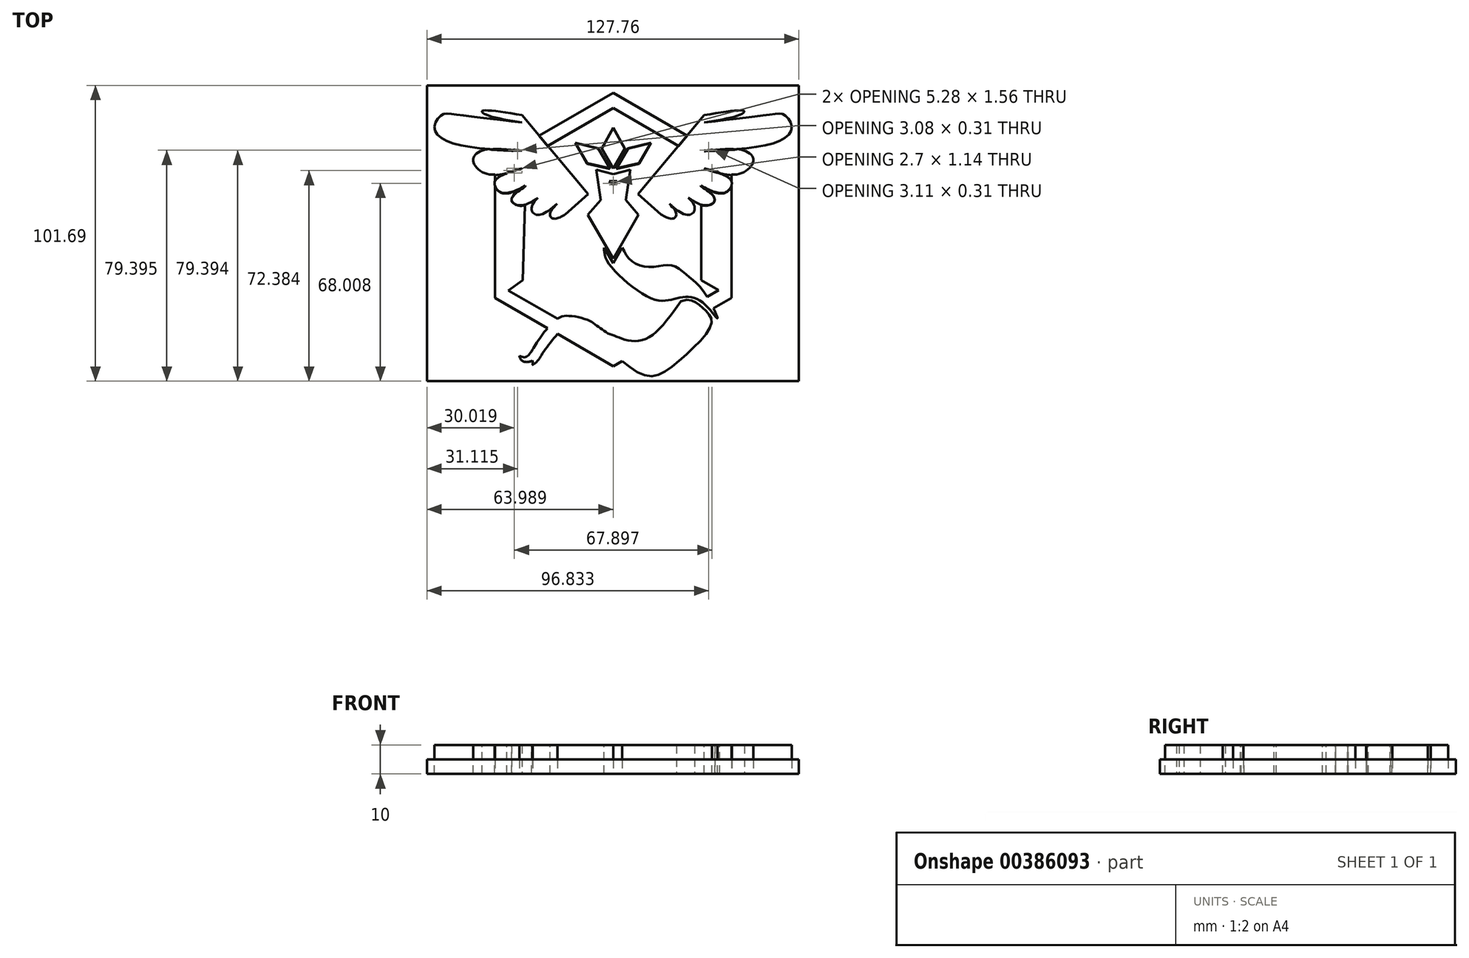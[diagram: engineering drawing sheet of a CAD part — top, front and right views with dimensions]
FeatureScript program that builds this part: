
annotation { "Feature Type Name" : "Feature", "Feature Type Description" : "" }
export const myFeature = defineFeature(function(context is Context, id is Id, definition is map)
    precondition{}
    {
        {
            var Q0;
            Q0=qCreatedBy(makeId("Top.planeOp"),FACE);
            var sketch = newSketch(context, id + "F0", { "sketchPlane" : qUnion([Q0])});
            skLineSegment(sketch, "E0.0", {"start": v(-34.42, 27.09) * mm, "end": v(-34.1, 27.27) * mm});
            skLineSegment(sketch, "E0.1", {"start": v(-0.03, 46.93) * mm, "end": v(25.45, 32.25) * mm});
            skLineSegment(sketch, "E0.2", {"start": v(40.64, 18.71) * mm, "end": v(40.62, -23.47) * mm});
            skLineSegment(sketch, "E0.3", {"start": v(40.62, -23.47) * mm, "end": v(34.43, -27.05) * mm});
            skLineSegment(sketch, "E0.4", {"start": v(-0.03, -46.93) * mm, "end": v(-19.17, -35.86) * mm});
            skLineSegment(sketch, "E0.5", {"start": v(-40.66, -23.44) * mm, "end": v(-40.66, 18.71) * mm});
            skLineSegment(sketch, "E1.1", {"start": v(-36.2, 20.89) * mm, "end": v(-36.18, 20.9) * mm});
            skLineSegment(sketch, "E1.2", {"start": v(-0.03, 41.74) * mm, "end": v(22.51, 28.74) * mm});
            skLineSegment(sketch, "E1.4", {"start": v(36.16, -20.84) * mm, "end": v(32.26, -23.1) * mm});
            skLineSegment(sketch, "E1.5", {"start": v(0.03, -41.74) * mm, "end": v(-0.03, -41.7) * mm});
            skLineSegment(sketch, "E2.0", {"start": v(-31.14, -17.38) * mm, "end": v(-30.4, 8.4) * mm});
            skLineSegment(sketch, "E2.3", {"start": v(30.15, 14.97) * mm, "end": v(30.15, 14.86) * mm});
            skLineSegment(sketch, "E3", {"start": v(-34.6, 19.99) * mm, "end": v(-34.47, 19.91) * mm});
            skLineSegment(sketch, "E4", {"start": v(-36.13, -20.9) * mm, "end": v(-31.14, -17.38) * mm});
            skLineSegment(sketch, "E5", {"start": v(36.16, -20.84) * mm, "end": v(30.18, -17.39) * mm});
            skLineSegment(sketch, "E6", {"start": v(34.42, 19.9) * mm, "end": v(34.55, 19.98) * mm});
            skLineSegment(sketch, "E7.1", {"start": v(8.6, 5.06) * mm, "end": v(-0.04, -10.05) * mm});
            skLineSegment(sketch, "E7.2", {"start": v(-0.04, -10.05) * mm, "end": v(-8.73, 5.03) * mm});
            skPoint(sketch, "E7.0.midPoint", {"position": v(-0.06, 5.04) * mm});
            skLineSegment(sketch, "E8", {"start": v(-8.73, 5.03) * mm, "end": v(-4.35, 10.2) * mm});
            skLineSegment(sketch, "E9", {"start": v(4.29, 10.2) * mm, "end": v(8.6, 5.06) * mm});
            skLineSegment(sketch, "E10", {"start": v(-0.03, 20.9) * mm, "end": v(-3.95, 27.84) * mm});
            skLineSegment(sketch, "E11", {"start": v(-3.95, 27.84) * mm, "end": v(-0.03, 34.95) * mm});
            skLineSegment(sketch, "E12", {"start": v(-0.03, 34.95) * mm, "end": v(3.92, 27.84) * mm});
            skLineSegment(sketch, "E13", {"start": v(3.92, 27.84) * mm, "end": v(-0.03, 20.9) * mm});
            skLineSegment(sketch, "E14", {"start": v(1.05, 20.86) * mm, "end": v(5.08, 27.84) * mm});
            skLineSegment(sketch, "E15", {"start": v(5.08, 27.84) * mm, "end": v(12.97, 29.67) * mm});
            skLineSegment(sketch, "E16", {"start": v(12.97, 29.67) * mm, "end": v(8.92, 22.65) * mm});
            skLineSegment(sketch, "E17", {"start": v(8.92, 22.65) * mm, "end": v(1.05, 20.86) * mm});
            skLineSegment(sketch, "E18", {"start": v(-0.03, 19.06) * mm, "end": v(5.8, 20.53) * mm});
            skLineSegment(sketch, "E19", {"start": v(5.8, 20.53) * mm, "end": v(4.29, 10.2) * mm});
            skLineSegment(sketch, "E20.MirrorCS", {"start": v(-1.11, 20.86) * mm, "end": v(-5.14, 27.84) * mm});
            skLineSegment(sketch, "E21.MirrorCS", {"start": v(36.13, 20.89) * mm, "end": v(36.12, 20.89) * mm});
            skLineSegment(sketch, "E22.MirrorCS", {"start": v(-8.98, 22.65) * mm, "end": v(-1.11, 20.86) * mm});
            skLineSegment(sketch, "E23.MirrorCS", {"start": v(-13.03, 29.67) * mm, "end": v(-8.98, 22.65) * mm});
            skLineSegment(sketch, "E24.MirrorCS", {"start": v(-5.14, 27.84) * mm, "end": v(-13.03, 29.67) * mm});
            skLineSegment(sketch, "E25.MirrorCS", {"start": v(-5.85, 20.53) * mm, "end": v(-4.35, 10.2) * mm});
            skLineSegment(sketch, "E26.MirrorCS", {"start": v(-0.03, 19.06) * mm, "end": v(-5.85, 20.53) * mm});
            skPoint(sketch, "E27.endSnap0", {"position": v(2.88, 19.8) * mm});
            skLineSegment(sketch, "E28", {"start": v(8.54, 12.07) * mm, "end": v(16.4, 5.06) * mm});
            skFitSpline(sketch, "E29", {"points": [v(16.4, 5.06) * mm, v(20.32, 3.6) * mm, v(21.7, 5.06) * mm, v(16.4, 11.34) * mm], "startDerivative": vector(12.83, -7.25) * mm, "endDerivative": vector(-17.45, 15.71) * mm});
            skFitSpline(sketch, "E30", {"points": [v(16.4, 11.34) * mm, v(24.02, 5.3) * mm, v(27.15, 5.3) * mm, v(27.86, 8) * mm, v(21.51, 14.15) * mm], "startDerivative": vector(24.54, -23.19) * mm, "endDerivative": vector(-27.7, 19.99) * mm});
            skFitSpline(sketch, "E31", {"points": [v(21.51, 14.15) * mm, v(31.76, 8.18) * mm, v(34.89, 10.17) * mm, v(27.63, 16.43) * mm], "startDerivative": vector(26.85, -21.95) * mm, "endDerivative": vector(-29.92, 18.45) * mm});
            skFitSpline(sketch, "E32", {"points": [v(27.63, 16.43) * mm, v(38.3, 12.59) * mm, v(40.63, 16.43) * mm, v(31.28, 20.89) * mm], "startDerivative": vector(31.14, -18.38) * mm, "endDerivative": vector(-35.14, 9.32) * mm});
            skFitSpline(sketch, "E33", {"points": [v(31.28, 20.89) * mm, v(43.86, 19.14) * mm, v(48.13, 23.83) * mm, v(44.57, 27.1) * mm, v(31.28, 26.96) * mm], "startDerivative": vector(45.87, -14.68) * mm, "endDerivative": vector(-48.56, -5.6) * mm});
            skFitSpline(sketch, "E34", {"points": [v(31.28, 26.96) * mm, v(57.1, 30.24) * mm, v(61.36, 35.08) * mm, v(58.94, 39.2) * mm, v(54.82, 39.49) * mm, v(31.28, 36.64) * mm], "startDerivative": vector(100.04, 4.04) * mm, "endDerivative": vector(-97.48, -11.56) * mm});
            skFitSpline(sketch, "E35", {"points": [v(31.28, 36.64) * mm, v(44.13, 39.57) * mm, v(44.99, 40.57) * mm, v(31.28, 39.2) * mm], "startDerivative": vector(37.5, 6.3) * mm, "endDerivative": vector(-44.89, -7.34) * mm});
            skFitSpline(sketch, "E36", {"points": [v(8.54, 12.07) * mm, v(31.28, 39.2) * mm], "startDerivative": vector(22.74, 27.13) * mm, "endDerivative": vector(22.74, 27.13) * mm});
            skLineSegment(sketch, "E37.trimOffspring", {"start": v(30.15, 8.44) * mm, "end": v(30.18, -17.39) * mm});
            skLineSegment(sketch, "E38.trimOffspring", {"start": v(36.12, 20.89) * mm, "end": v(36.13, 20.9) * mm});
            skLineSegment(sketch, "E39.trimOffspring", {"start": v(34.07, 27.28) * mm, "end": v(34.39, 27.1) * mm});
            skFitSpline(sketch, "E40.MirrorCS", {"points": [v(-8.6, 12.07) * mm, v(-31.34, 39.2) * mm], "startDerivative": vector(-22.74, 27.13) * mm, "endDerivative": vector(-22.74, 27.13) * mm});
            skLineSegment(sketch, "E41.MirrorCS", {"start": v(-8.6, 12.07) * mm, "end": v(-16.47, 5.06) * mm});
            skFitSpline(sketch, "E42.MirrorCS", {"points": [v(-16.47, 5.06) * mm, v(-20.38, 3.6) * mm, v(-21.76, 5.06) * mm, v(-16.47, 11.34) * mm], "startDerivative": vector(-12.83, -7.25) * mm, "endDerivative": vector(17.45, 15.71) * mm});
            skFitSpline(sketch, "E43.MirrorCS", {"points": [v(-16.47, 11.34) * mm, v(-24.08, 5.3) * mm, v(-27.21, 5.3) * mm, v(-27.93, 8) * mm, v(-21.57, 14.15) * mm], "startDerivative": vector(-24.54, -23.19) * mm, "endDerivative": vector(27.7, 19.99) * mm});
            skFitSpline(sketch, "E44.MirrorCS", {"points": [v(-21.57, 14.15) * mm, v(-31.82, 8.18) * mm, v(-34.95, 10.17) * mm, v(-27.7, 16.43) * mm], "startDerivative": vector(-26.85, -21.95) * mm, "endDerivative": vector(29.92, 18.45) * mm});
            skFitSpline(sketch, "E45.MirrorCS", {"points": [v(-27.7, 16.43) * mm, v(-38.37, 12.59) * mm, v(-40.7, 16.43) * mm, v(-31.34, 20.89) * mm], "startDerivative": vector(-31.14, -18.38) * mm, "endDerivative": vector(35.14, 9.32) * mm});
            skFitSpline(sketch, "E46.MirrorCS", {"points": [v(-31.34, 20.89) * mm, v(-43.92, 19.14) * mm, v(-48.19, 23.83) * mm, v(-44.63, 27.1) * mm, v(-31.34, 26.96) * mm], "startDerivative": vector(-45.87, -14.68) * mm, "endDerivative": vector(48.56, -5.6) * mm});
            skFitSpline(sketch, "E47.MirrorCS", {"points": [v(-31.34, 26.96) * mm, v(-57.15, 30.24) * mm, v(-61.42, 35.08) * mm, v(-59, 39.2) * mm, v(-54.88, 39.49) * mm, v(-31.34, 36.64) * mm], "startDerivative": vector(-100.04, 4.04) * mm, "endDerivative": vector(97.48, -11.56) * mm});
            skFitSpline(sketch, "E48.MirrorCS", {"points": [v(-31.34, 36.64) * mm, v(-44.2, 39.57) * mm, v(-45.05, 40.57) * mm, v(-31.34, 39.2) * mm], "startDerivative": vector(-37.5, 6.3) * mm, "endDerivative": vector(44.89, -7.34) * mm});
            skLineSegment(sketch, "E49.trimOffspring", {"start": v(-36.18, 20.9) * mm, "end": v(-36.2, 20.9) * mm});
            skLineSegment(sketch, "E50.trimOffspring", {"start": v(-25.5, 32.24) * mm, "end": v(-0.03, 46.93) * mm});
            skLineSegment(sketch, "E51.trimOffspring", {"start": v(-22.57, 28.74) * mm, "end": v(-0.03, 41.74) * mm});
            skLineSegment(sketch, "E52.trimOffspring", {"start": v(-30.2, 14.86) * mm, "end": v(-30.2, 14.97) * mm});
            skLineSegment(sketch, "E53", {"start": v(-0.03, -11.6) * mm, "end": v(3.06, -6.2) * mm});
            skLineSegment(sketch, "E54.MirrorCS", {"start": v(-0.03, -11.6) * mm, "end": v(-3.12, -6.2) * mm});
            skFitSpline(sketch, "E55", {"points": [v(3.06, -6.2) * mm, v(6.6, -11.02) * mm, v(13.43, -12.87) * mm, v(20.12, -12.3) * mm, v(25.39, -15.72) * mm, v(31.36, -21.7) * mm, v(35.78, -30.52) * mm, v(29.9, -24.46) * mm, v(20.83, -23.83) * mm], "startDerivative": vector(25.23, -49.18) * mm, "endDerivative": vector(-67.6, -14.69) * mm});
            skFitSpline(sketch, "E56", {"points": [v(20.83, -23.83) * mm, v(13.57, -23.83) * mm, v(-1.8, -11.3) * mm, v(-3.12, -6.2) * mm], "startDerivative": vector(-22.06, -5.97) * mm, "endDerivative": vector(0.15, 18.4) * mm});
            skFitSpline(sketch, "E57", {"points": [v(23.25, -24.69) * mm, v(28.58, -25.22) * mm, v(32.22, -28.32) * mm, v(33.78, -32.23) * mm, v(22.97, -44.75) * mm, v(11.01, -50.16) * mm, v(-5.4, -38.6) * mm], "startDerivative": vector(57.83, 25.3) * mm, "endDerivative": vector(-68.09, 39.24) * mm});
            skFitSpline(sketch, "E58", {"points": [v(23.25, -24.69) * mm, v(10.3, -37.92) * mm, v(2.19, -37.21) * mm, v(-1.94, -35.65) * mm], "startDerivative": vector(-29.4, -41.34) * mm, "endDerivative": vector(-18.15, 5.69) * mm});
            skLineSegment(sketch, "E59.trimOffspring", {"start": v(3.03, -45.17) * mm, "end": v(-0.03, -46.93) * mm});
            skFitSpline(sketch, "E60", {"points": [v(-1.94, -35.65) * mm, v(-5.4, -33.23) * mm, v(-8.95, -31.03) * mm, v(-16.57, -29.68) * mm, v(-19.2, -30.65) * mm], "startDerivative": vector(-15, 10.15) * mm, "endDerivative": vector(-10.84, -6.57) * mm});
            skFitSpline(sketch, "E61", {"points": [v(-19.2, -30.65) * mm, v(-21.65, -32.72) * mm, v(-26.22, -38.82) * mm, v(-28.75, -42.7) * mm, v(-30.45, -43.9) * mm, v(-32.3, -43.39) * mm], "startDerivative": vector(-12.13, -8.75) * mm, "endDerivative": vector(-13.1, 6) * mm});
            skFitSpline(sketch, "E62", {"points": [v(-32.3, -43.39) * mm, v(-31.67, -44.82) * mm, v(-29.8, -45.54) * mm, v(-27.77, -45) * mm], "startDerivative": vector(1.27, -5.16) * mm, "endDerivative": vector(5.63, 2.32) * mm});
            skFitSpline(sketch, "E63", {"points": [v(-27.77, -45) * mm, v(-27.77, -46.38) * mm, v(-27.77, -46.5) * mm, v(-26.15, -45.27) * mm, v(-24.42, -42.7) * mm, v(-19.75, -36.56) * mm, v(-16.46, -33.51) * mm, v(-12.5, -33.57) * mm, v(-5.4, -38.6) * mm], "startDerivative": vector(0.74, -21.08) * mm, "endDerivative": vector(36.31, -31.02) * mm});
            skLineSegment(sketch, "E64.trimOffspring", {"start": v(-22.64, -33.86) * mm, "end": v(-40.66, -23.44) * mm});
            skLineSegment(sketch, "E65.trimOffspring", {"start": v(-19.2, -30.65) * mm, "end": v(-36.13, -20.9) * mm});
            skLineSegment(sketch, "E66.trimOffspring", {"start": v(-0.03, -41.7) * mm, "end": v(-0.03, -42.57) * mm});
            skLineSegment(sketch, "E67", {"start": v(-0.03, 15.32) * mm, "end": v(1.32, 16.46) * mm});
            skLineSegment(sketch, "E68", {"start": v(1.32, 16.46) * mm, "end": v(-0.03, 16.46) * mm});
            skLineSegment(sketch, "E69.MirrorCS", {"start": v(-1.38, 16.46) * mm, "end": v(-0.03, 16.46) * mm});
            skLineSegment(sketch, "E70.MirrorCS", {"start": v(-0.03, 15.32) * mm, "end": v(-1.38, 16.46) * mm});
            skSolve(sketch);
        }
        {
            var Q0;
            Q0=makeQuery(id+"F0.imprint","IMPRINT",FACE,{"disambiguationData":[TD([[makeQuery(id+"F0.imprint","IMPRINT",EDGE,{"derivedFrom":sQuery(id+"F0.wireOp",EDGE,"E7.1")}),-1.0]])]});
            var Q1;
            {var subQ3=sQuery(id+"F0.wireOp",EDGE,"E53");Q1=makeQuery(id+"F0.imprint","IMPRINT",FACE,{"disambiguationData":[TD([[makeQuery(id+"F0.imprint","IMPRINT",EDGE,{"derivedFrom":subQ3}),-1.0]])]});}
            var Q2;
            {var subQ0=sQuery(id+"F0.wireOp",EDGE,"E58");Q2=makeQuery(id+"F0.imprint","IMPRINT",FACE,{"disambiguationData":[TD([[makeQuery(id+"F0.imprint","IMPRINT",EDGE,{"derivedFrom":subQ0}),1.0]])]});}
            var Q3;
            Q3=makeQuery(id+"F0.imprint","IMPRINT",FACE,{"disambiguationData":[TD([[makeQuery(id+"F0.imprint","IMPRINT",EDGE,{"derivedFrom":sQuery(id+"F0.wireOp",EDGE,"E10")}),-1.0]])]});
            var Q4;
            Q4=makeQuery(id+"F0.imprint","IMPRINT",FACE,{"disambiguationData":[TD([[makeQuery(id+"F0.imprint","IMPRINT",EDGE,{"derivedFrom":sQuery(id+"F0.wireOp",EDGE,"E20.MirrorCS")}),1.0]])]});
            var Q5;
            Q5=makeQuery(id+"F0.imprint","IMPRINT",FACE,{"disambiguationData":[TD([[makeQuery(id+"F0.imprint","IMPRINT",EDGE,{"derivedFrom":sQuery(id+"F0.wireOp",EDGE,"E14")}),-1.0]])]});
            var Q6;
            {var subQ4=sQuery(id+"F0.wireOp",EDGE,"E0.1");Q6=makeQuery(id+"F0.imprint","IMPRINT",FACE,{"disambiguationData":[TD([[makeQuery(id+"F0.imprint","IMPRINT",EDGE,{"derivedFrom":subQ4}),-1.0]])]});}
            var Q7;
            {var subQ4=sQuery(id+"F0.wireOp",EDGE,"E0.3");Q7=makeQuery(id+"F0.imprint","IMPRINT",FACE,{"disambiguationData":[TD([[makeQuery(id+"F0.imprint","IMPRINT",EDGE,{"derivedFrom":subQ4}),-1.0]])]});}
            var Q8;
            {var subQ1=sQuery(id+"F0.wireOp",EDGE,"E2.0");Q8=makeQuery(id+"F0.imprint","IMPRINT",FACE,{"disambiguationData":[TD([[makeQuery(id+"F0.imprint","IMPRINT",EDGE,{"derivedFrom":subQ1}),1.0]])]});}
            var Q9;
            {var subQ5=sQuery(id+"F0.wireOp",EDGE,"E0.4");Q9=makeQuery(id+"F0.imprint","IMPRINT",FACE,{"disambiguationData":[TD([[makeQuery(id+"F0.imprint","IMPRINT",EDGE,{"derivedFrom":subQ5}),-1.0]])]});}
            var Q10;
            {var subQ0=sQuery(id+"F0.wireOp",EDGE,"E46.MirrorCS");var subQ1=sQuery(id+"F0.wireOp",EDGE,"E0.5");var subQ2=makeQuery(id+"F0.imprint","INTERSECT",VERTEX,{"derivedFrom":[subQ1,subQ0]});Q10=makeQuery(id+"F0.imprint","IMPRINT",FACE,{"disambiguationData":[TD([[makeQuery(id+"F0.imprint","IMPRINT",EDGE,{"disambiguationData":[TD([[subQ2,1.0]])],"derivedFrom":subQ1}),-1.0]])]});}
            var Q11;
            {var subQ0=sQuery(id+"F0.wireOp",EDGE,"E0.0");Q11=makeQuery(id+"F0.imprint","IMPRINT",FACE,{"disambiguationData":[TD([[makeQuery(id+"F0.imprint","IMPRINT",EDGE,{"derivedFrom":subQ0}),1.0]])]});}
            var Q12;
            {var subQ0=sQuery(id+"F0.wireOp",EDGE,"E33");var subQ1=sQuery(id+"F0.wireOp",EDGE,"E0.2");var subQ2=makeQuery(id+"F0.imprint","INTERSECT",VERTEX,{"derivedFrom":[subQ1,subQ0]});Q12=makeQuery(id+"F0.imprint","IMPRINT",FACE,{"disambiguationData":[TD([[makeQuery(id+"F0.imprint","IMPRINT",EDGE,{"disambiguationData":[TD([[subQ2,-1.0]])],"derivedFrom":subQ1}),-1.0]])]});}
            var Q13;
            {var subQ0=sQuery(id+"F0.wireOp",EDGE,"E6");Q13=makeQuery(id+"F0.imprint","IMPRINT",FACE,{"disambiguationData":[TD([[makeQuery(id+"F0.imprint","IMPRINT",EDGE,{"derivedFrom":subQ0}),1.0]])]});}
            var Q14;
            {var subQ0=sQuery(id+"F0.wireOp",EDGE,"E6");Q14=makeQuery(id+"F0.imprint","IMPRINT",FACE,{"disambiguationData":[TD([[makeQuery(id+"F0.imprint","IMPRINT",EDGE,{"derivedFrom":subQ0}),-1.0]])]});}
            var Q15;
            {var subQ0=sQuery(id+"F0.wireOp",EDGE,"E39.trimOffspring");Q15=makeQuery(id+"F0.imprint","IMPRINT",FACE,{"disambiguationData":[TD([[makeQuery(id+"F0.imprint","IMPRINT",EDGE,{"derivedFrom":subQ0}),1.0]])]});}
            var Q16;
            {var subQ3=sQuery(id+"F0.wireOp",EDGE,"E39.trimOffspring");Q16=makeQuery(id+"F0.imprint","IMPRINT",FACE,{"disambiguationData":[TD([[makeQuery(id+"F0.imprint","IMPRINT",EDGE,{"derivedFrom":subQ3}),-1.0]])]});}
            extrude(context, id + "F1", {"entities" : qUnion([Q0, Q1, Q2, Q3, Q4, Q5, Q6, Q7, Q8, Q9, Q10, Q11, Q12, Q13, Q14, Q15, Q16]), "depth" : 10 * mm});
        }
        {
            var Q0;
            Q0=qCreatedBy(makeId("Top.planeOp"),FACE);
            var sketch = newSketch(context, id + "F2", { "sketchPlane" : qUnion([Q0])});
            skLineSegment(sketch, "E71.0", {"start": v(-34.44, 27.25) * mm, "end": v(-34.13, 27.43) * mm});
            skLineSegment(sketch, "E71.1", {"start": v(-0.04, -47.04) * mm, "end": v(-25.52, -32.35) * mm});
            skLineSegment(sketch, "E71.2", {"start": v(-40.7, -18.82) * mm, "end": v(-40.7, 23.37) * mm});
            skLineSegment(sketch, "E71.5", {"start": v(40.58, 23.33) * mm, "end": v(40.59, -18.82) * mm});
            skLineSegment(sketch, "E72.1", {"start": v(-36.22, 21.04) * mm, "end": v(-36.2, 21.05) * mm});
            skLineSegment(sketch, "E72.2", {"start": v(-0.05, 41.9) * mm, "end": v(22.49, 28.9) * mm});
            skLineSegment(sketch, "E73.3", {"start": v(30.12, 15.12) * mm, "end": v(30.12, 15.01) * mm});
            skLineSegment(sketch, "E74", {"start": v(-34.63, 20.14) * mm, "end": v(-34.5, 20.07) * mm});
            skLineSegment(sketch, "E75", {"start": v(34.4, 20.06) * mm, "end": v(34.53, 20.14) * mm});
            skPoint(sketch, "E76.0.midPoint", {"position": v(-0.08, 5.2) * mm});
            skLineSegment(sketch, "E77", {"start": v(-8.75, 5.18) * mm, "end": v(-4.37, 10.36) * mm});
            skLineSegment(sketch, "E78", {"start": v(4.26, 10.35) * mm, "end": v(8.58, 5.22) * mm});
            skLineSegment(sketch, "E79", {"start": v(-0.05, 21.05) * mm, "end": v(-3.97, 28) * mm});
            skLineSegment(sketch, "E80", {"start": v(-3.97, 28) * mm, "end": v(-0.05, 35.1) * mm});
            skLineSegment(sketch, "E81", {"start": v(-0.05, 35.1) * mm, "end": v(3.9, 28) * mm});
            skLineSegment(sketch, "E82", {"start": v(3.9, 28) * mm, "end": v(-0.05, 21.05) * mm});
            skLineSegment(sketch, "E83", {"start": v(1.03, 21.02) * mm, "end": v(5.05, 28) * mm});
            skLineSegment(sketch, "E84", {"start": v(5.05, 28) * mm, "end": v(12.94, 29.83) * mm});
            skLineSegment(sketch, "E85", {"start": v(12.94, 29.83) * mm, "end": v(8.9, 22.8) * mm});
            skLineSegment(sketch, "E86", {"start": v(8.9, 22.8) * mm, "end": v(1.03, 21.02) * mm});
            skLineSegment(sketch, "E87", {"start": v(-0.05, 19.21) * mm, "end": v(5.77, 20.69) * mm});
            skLineSegment(sketch, "E88", {"start": v(5.77, 20.69) * mm, "end": v(4.26, 10.35) * mm});
            skLineSegment(sketch, "E89.MirrorCS", {"start": v(-1.14, 21.02) * mm, "end": v(-5.16, 28) * mm});
            skLineSegment(sketch, "E90.MirrorCS", {"start": v(36.11, 21.04) * mm, "end": v(36.1, 21.04) * mm});
            skLineSegment(sketch, "E91.MirrorCS", {"start": v(-9, 22.8) * mm, "end": v(-1.14, 21.02) * mm});
            skLineSegment(sketch, "E92.MirrorCS", {"start": v(-13.05, 29.83) * mm, "end": v(-9, 22.8) * mm});
            skLineSegment(sketch, "E93.MirrorCS", {"start": v(-5.16, 28) * mm, "end": v(-13.05, 29.83) * mm});
            skLineSegment(sketch, "E94.MirrorCS", {"start": v(-5.88, 20.69) * mm, "end": v(-4.37, 10.35) * mm});
            skLineSegment(sketch, "E95.MirrorCS", {"start": v(-0.05, 19.21) * mm, "end": v(-5.88, 20.69) * mm});
            skPoint(sketch, "E96.endSnap0", {"position": v(2.86, 19.95) * mm});
            skLineSegment(sketch, "E97", {"start": v(8.52, 12.23) * mm, "end": v(16.39, 5.22) * mm});
            skFitSpline(sketch, "E98", {"points": [v(16.39, 5.22) * mm, v(20.3, 3.75) * mm, v(21.68, 5.22) * mm, v(16.39, 11.5) * mm], "startDerivative": vector(12.83, -7.25) * mm, "endDerivative": vector(-17.45, 15.71) * mm});
            skFitSpline(sketch, "E99", {"points": [v(16.39, 11.5) * mm, v(24, 5.45) * mm, v(27.13, 5.45) * mm, v(27.84, 8.15) * mm, v(21.49, 14.3) * mm], "startDerivative": vector(24.54, -23.19) * mm, "endDerivative": vector(-27.7, 19.99) * mm});
            skFitSpline(sketch, "E100", {"points": [v(21.49, 14.3) * mm, v(31.74, 8.33) * mm, v(34.87, 10.32) * mm, v(27.6, 16.59) * mm], "startDerivative": vector(26.85, -21.95) * mm, "endDerivative": vector(-29.92, 18.45) * mm});
            skFitSpline(sketch, "E101", {"points": [v(27.6, 16.59) * mm, v(38.28, 12.74) * mm, v(40.61, 16.59) * mm, v(31.26, 21.04) * mm], "startDerivative": vector(31.14, -18.38) * mm, "endDerivative": vector(-35.14, 9.32) * mm});
            skFitSpline(sketch, "E102", {"points": [v(31.26, 21.04) * mm, v(43.83, 19.3) * mm, v(48.1, 23.99) * mm, v(44.55, 27.26) * mm, v(31.26, 27.12) * mm], "startDerivative": vector(45.87, -14.68) * mm, "endDerivative": vector(-48.56, -5.6) * mm});
            skFitSpline(sketch, "E103", {"points": [v(31.26, 27.12) * mm, v(57.07, 30.4) * mm, v(61.34, 35.23) * mm, v(58.92, 39.36) * mm, v(54.8, 39.64) * mm, v(31.26, 36.8) * mm], "startDerivative": vector(100.04, 4.04) * mm, "endDerivative": vector(-97.48, -11.56) * mm});
            skFitSpline(sketch, "E104", {"points": [v(31.26, 36.8) * mm, v(44.1, 39.73) * mm, v(44.96, 40.72) * mm, v(31.26, 39.36) * mm], "startDerivative": vector(37.5, 6.3) * mm, "endDerivative": vector(-44.89, -7.34) * mm});
            skFitSpline(sketch, "E105", {"points": [v(8.52, 12.23) * mm, v(31.26, 39.36) * mm], "startDerivative": vector(22.74, 27.13) * mm, "endDerivative": vector(22.74, 27.13) * mm});
            skLineSegment(sketch, "E106.trimOffspring", {"start": v(36.1, 21.04) * mm, "end": v(36.1, 21.05) * mm});
            skLineSegment(sketch, "E107.trimOffspring", {"start": v(34.05, 27.43) * mm, "end": v(34.37, 27.25) * mm});
            skFitSpline(sketch, "E108.MirrorCS", {"points": [v(-8.62, 12.23) * mm, v(-31.36, 39.36) * mm], "startDerivative": vector(-22.74, 27.13) * mm, "endDerivative": vector(-22.74, 27.13) * mm});
            skLineSegment(sketch, "E109.MirrorCS", {"start": v(-8.62, 12.23) * mm, "end": v(-16.5, 5.22) * mm});
            skFitSpline(sketch, "E110.MirrorCS", {"points": [v(-16.5, 5.22) * mm, v(-20.4, 3.75) * mm, v(-21.78, 5.22) * mm, v(-16.5, 11.5) * mm], "startDerivative": vector(-12.83, -7.25) * mm, "endDerivative": vector(17.45, 15.71) * mm});
            skFitSpline(sketch, "E111.MirrorCS", {"points": [v(-16.5, 11.5) * mm, v(-24.1, 5.45) * mm, v(-27.23, 5.45) * mm, v(-27.95, 8.15) * mm, v(-21.6, 14.3) * mm], "startDerivative": vector(-24.54, -23.19) * mm, "endDerivative": vector(27.7, 19.99) * mm});
            skFitSpline(sketch, "E112.MirrorCS", {"points": [v(-21.6, 14.3) * mm, v(-31.84, 8.33) * mm, v(-34.97, 10.32) * mm, v(-27.71, 16.59) * mm], "startDerivative": vector(-26.85, -21.95) * mm, "endDerivative": vector(29.92, 18.45) * mm});
            skFitSpline(sketch, "E113.MirrorCS", {"points": [v(-27.71, 16.59) * mm, v(-38.39, 12.74) * mm, v(-40.72, 16.59) * mm, v(-31.36, 21.04) * mm], "startDerivative": vector(-31.14, -18.38) * mm, "endDerivative": vector(35.14, 9.32) * mm});
            skFitSpline(sketch, "E114.MirrorCS", {"points": [v(-31.36, 21.04) * mm, v(-43.94, 19.3) * mm, v(-48.2, 23.99) * mm, v(-44.65, 27.26) * mm, v(-31.36, 27.12) * mm], "startDerivative": vector(-45.87, -14.68) * mm, "endDerivative": vector(48.56, -5.6) * mm});
            skFitSpline(sketch, "E115.MirrorCS", {"points": [v(-31.36, 27.12) * mm, v(-57.18, 30.4) * mm, v(-61.45, 35.23) * mm, v(-59.03, 39.36) * mm, v(-54.9, 39.64) * mm, v(-31.36, 36.8) * mm], "startDerivative": vector(-100.04, 4.04) * mm, "endDerivative": vector(97.48, -11.56) * mm});
            skFitSpline(sketch, "E116.MirrorCS", {"points": [v(-31.36, 36.8) * mm, v(-44.21, 39.73) * mm, v(-45.07, 40.72) * mm, v(-31.36, 39.36) * mm], "startDerivative": vector(-37.5, 6.3) * mm, "endDerivative": vector(44.89, -7.34) * mm});
            skLineSegment(sketch, "E117.trimOffspring", {"start": v(-36.2, 21.05) * mm, "end": v(-36.21, 21.05) * mm});
            skLineSegment(sketch, "E118.trimOffspring", {"start": v(-22.6, 28.9) * mm, "end": v(-0.05, 41.9) * mm});
            skLineSegment(sketch, "E119.trimOffspring", {"start": v(-30.23, 15.02) * mm, "end": v(-30.22, 15.13) * mm});
            skLineSegment(sketch, "E120", {"start": v(-0.05, 15.47) * mm, "end": v(1.3, 16.61) * mm});
            skLineSegment(sketch, "E121", {"start": v(1.3, 16.61) * mm, "end": v(-0.05, 16.61) * mm});
            skLineSegment(sketch, "E122.MirrorCS", {"start": v(-1.4, 16.61) * mm, "end": v(-0.05, 16.61) * mm});
            skLineSegment(sketch, "E123.MirrorCS", {"start": v(-0.05, 15.47) * mm, "end": v(-1.4, 16.61) * mm});
            skSolve(sketch);
        }
        {
            var Q0;
            Q0 = qSketchRegion(id + "F2", true);
            extrude(context, id + "F3", {"entities" : qUnion([Q0]), "depth" : 10 * mm});
        }
        {
            var Q0;
            Q0=qCreatedBy(makeId("Top.planeOp"),FACE);
            var sketch = newSketch(context, id + "F4", { "sketchPlane" : qUnion([Q0])});
            skLineSegment(sketch, "E124.bottom", {"start": v(-64.02, 49.57) * mm, "end": v(63.74, 49.57) * mm});
            skLineSegment(sketch, "E124.top", {"start": v(-64.02, -52.12) * mm, "end": v(63.74, -52.12) * mm});
            skLineSegment(sketch, "E124.left", {"start": v(-64.02, 49.57) * mm, "end": v(-64.02, -52.12) * mm});
            skLineSegment(sketch, "E124.right", {"start": v(63.74, 49.57) * mm, "end": v(63.74, -52.12) * mm});
            skSolve(sketch);
        }
        {
            var Q0;
            Q0 = qSketchRegion(id + "F4", true);
            extrude(context, id + "F5", {"entities" : qUnion([Q0]), "depth" : 5 * mm});
        }
    });
